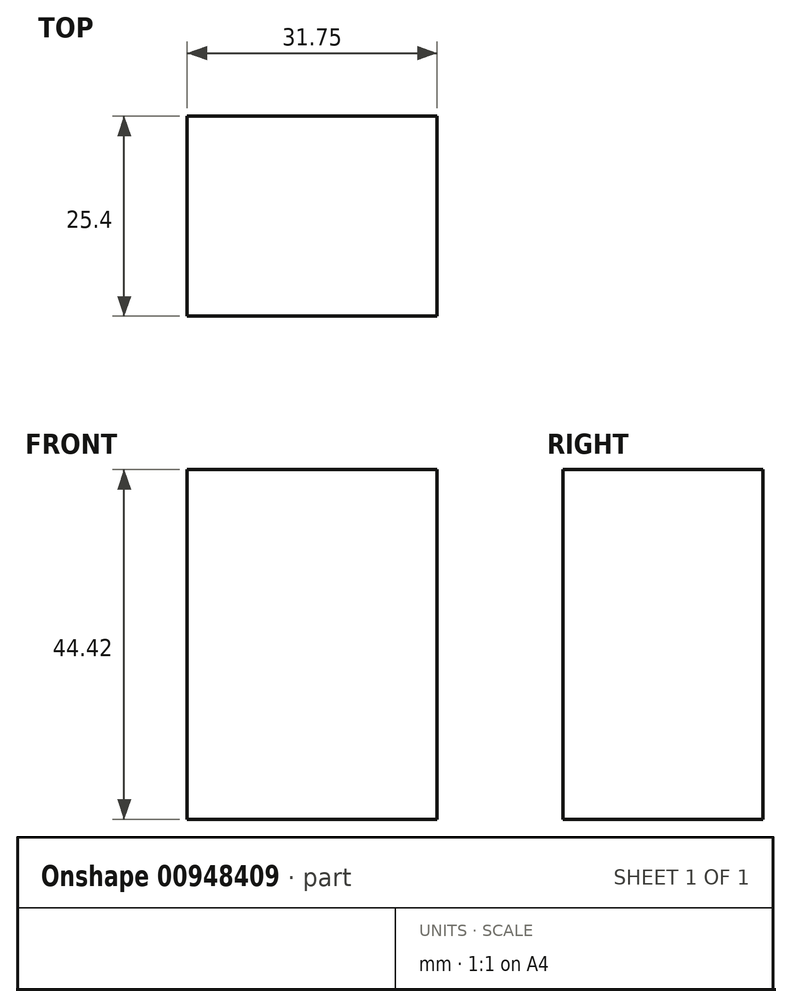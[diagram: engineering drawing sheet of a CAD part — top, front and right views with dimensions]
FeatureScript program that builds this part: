
annotation { "Feature Type Name" : "Feature", "Feature Type Description" : "" }
export const myFeature = defineFeature(function(context is Context, id is Id, definition is map)
    precondition{}
    {
        {
            var Q0;
            Q0=qCreatedBy(makeId("Front.planeOp"),FACE);
            var sketch = newSketch(context, id + "F0", { "sketchPlane" : qUnion([Q0])});
            skLineSegment(sketch, "E0.bottom", {"start": v(-31.75, 44.42) * mm, "end": v(0, 44.42) * mm});
            skLineSegment(sketch, "E0.top", {"start": v(-31.75, 0) * mm, "end": v(0, 0) * mm});
            skLineSegment(sketch, "E0.left", {"start": v(-31.75, 44.42) * mm, "end": v(-31.75, 0) * mm});
            skLineSegment(sketch, "E0.right", {"start": v(0, 44.42) * mm, "end": v(0, 0) * mm});
            skSolve(sketch);
        }
        {
            var Q0;
            Q0 = qSketchRegion(id + "F0", true);
            extrude(context, id + "F1", {"entities" : qUnion([Q0]), "depth" : 25.4 * mm, "offsetDistance" : 25.4 * mm});
        }
    });
